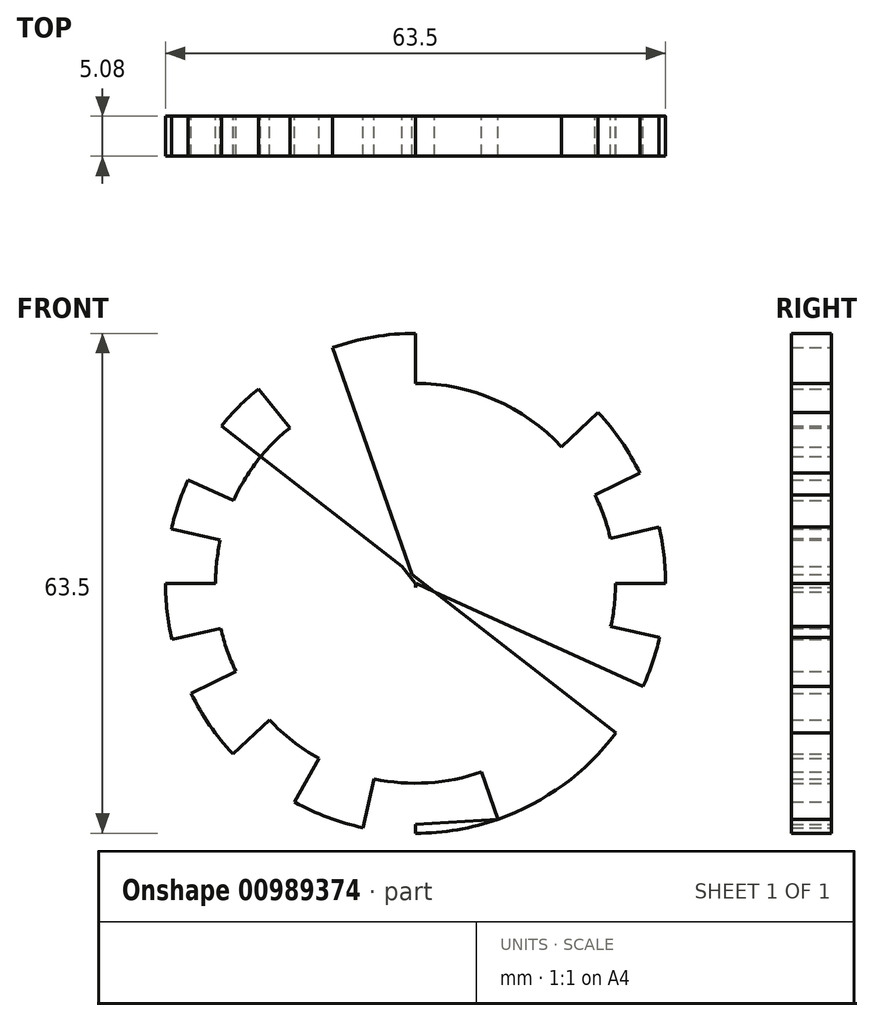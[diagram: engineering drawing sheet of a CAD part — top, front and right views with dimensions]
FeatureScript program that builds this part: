
annotation { "Feature Type Name" : "Feature", "Feature Type Description" : "" }
export const myFeature = defineFeature(function(context is Context, id is Id, definition is map)
    precondition{}
    {
        {
            var Q0;
            Q0=qCreatedBy(makeId("Front.planeOp"),FACE);
            var sketch = newSketch(context, id + "F0", { "sketchPlane" : qUnion([Q0])});
            skCircle(sketch, "E0", {"center": v(0, 0) * mm, "radius": 31.75 * mm});
            skLineSegment(sketch, "E1", {"start": v(-31.75, 0) * mm, "end": v(31.75, 0) * mm});
            skLineSegment(sketch, "E2", {"start": v(-19.95, 24.7) * mm, "end": v(19.95, -24.7) * mm});
            skLineSegment(sketch, "E3", {"start": v(-15.35, -27.8) * mm, "end": v(15.35, 27.8) * mm});
            skCircle(sketch, "E4", {"center": v(0, 0) * mm, "radius": 25.4 * mm});
            skLineSegment(sketch, "E5", {"start": v(-28.91, 13.12) * mm, "end": v(28.91, -13.12) * mm});
            skLineSegment(sketch, "E6", {"start": v(-28.5, -14) * mm, "end": v(28.5, 14) * mm});
            skLineSegment(sketch, "E7", {"start": v(0, -31.75) * mm, "end": v(0, 31.75) * mm});
            skLineSegment(sketch, "E8", {"start": v(-10.56, 29.94) * mm, "end": v(10.5, -29.96) * mm});
            skLineSegment(sketch, "E9", {"start": v(10.5, -29.96) * mm, "end": v(-6.65, -31.04) * mm});
            skLineSegment(sketch, "E10", {"start": v(-6.65, -31.04) * mm, "end": v(6.89, 31) * mm});
            skLineSegment(sketch, "E11", {"start": v(-23.2, -21.67) * mm, "end": v(23.2, 21.67) * mm});
            skLineSegment(sketch, "E12", {"start": v(-30.94, -7.14) * mm, "end": v(30.94, 7.14) * mm});
            skLineSegment(sketch, "E13", {"start": v(-24.67, 19.99) * mm, "end": v(25.43, -19) * mm});
            skLineSegment(sketch, "E14", {"start": v(-31, 6.88) * mm, "end": v(31, -6.88) * mm});
            skSolve(sketch);
        }
        {
            var Q0;
            {var subQ0=sQuery(id+"F0.wireOp",EDGE,"E4");var subQ1=sQuery(id+"F0.wireOp",EDGE,"E3");var subQ2=makeQuery(id+"F0.imprint","INTERSECT",VERTEX,{"disambiguationData":[OD(0.0)],"derivedFrom":[subQ1,subQ0]});Q0=makeQuery(id+"F0.imprint","IMPRINT",FACE,{"disambiguationData":[TD([[makeQuery(id+"F0.imprint","IMPRINT",EDGE,{"disambiguationData":[TD([[subQ2,-1.0]])],"derivedFrom":subQ1}),1.0]])]});}
            var Q1;
            {var subQ1=sQuery(id+"F0.wireOp",EDGE,"E3");var subQ7=sQuery(id+"F0.wireOp",EDGE,"E4");var subQ9=makeQuery(id+"F0.imprint","INTERSECT",VERTEX,{"disambiguationData":[OD(0.0)],"derivedFrom":[subQ1,subQ7]});Q1=makeQuery(id+"F0.imprint","IMPRINT",FACE,{"disambiguationData":[TD([[makeQuery(id+"F0.imprint","IMPRINT",EDGE,{"disambiguationData":[TD([[subQ9,-1.0]])],"derivedFrom":subQ1}),-1.0]])]});}
            var Q2;
            {var subQ0=sQuery(id+"F0.wireOp",EDGE,"E10");var subQ1=sQuery(id+"F0.wireOp",EDGE,"E4");var subQ2=makeQuery(id+"F0.imprint","INTERSECT",VERTEX,{"disambiguationData":[OD(1.0)],"derivedFrom":[subQ1,subQ0]});Q2=makeQuery(id+"F0.imprint","IMPRINT",FACE,{"disambiguationData":[TD([[makeQuery(id+"F0.imprint","IMPRINT",EDGE,{"disambiguationData":[TD([[subQ2,-1.0]])],"derivedFrom":subQ1}),1.0]])]});}
            var Q3;
            {var subQ0=sQuery(id+"F0.wireOp",EDGE,"E7");var subQ1=sQuery(id+"F0.wireOp",EDGE,"E4");var subQ2=makeQuery(id+"F0.imprint","INTERSECT",VERTEX,{"disambiguationData":[OD(1.0)],"derivedFrom":[subQ1,subQ0]});Q3=makeQuery(id+"F0.imprint","IMPRINT",FACE,{"disambiguationData":[TD([[makeQuery(id+"F0.imprint","IMPRINT",EDGE,{"disambiguationData":[TD([[subQ2,-1.0]])],"derivedFrom":subQ1}),1.0]])]});}
            var Q4;
            {var subQ0=sQuery(id+"F0.wireOp",EDGE,"E10");var subQ1=sQuery(id+"F0.wireOp",EDGE,"E2");var subQ2=makeQuery(id+"F0.imprint","INTERSECT",VERTEX,{"derivedFrom":[subQ1,subQ0]});Q4=makeQuery(id+"F0.imprint","IMPRINT",FACE,{"disambiguationData":[TD([[makeQuery(id+"F0.imprint","IMPRINT",EDGE,{"disambiguationData":[TD([[subQ2,-1.0]])],"derivedFrom":subQ1}),-1.0]])]});}
            var Q5;
            {var subQ0=sQuery(id+"F0.wireOp",EDGE,"E10");var subQ6=sQuery(id+"F0.wireOp",EDGE,"E2");var subQ9=makeQuery(id+"F0.imprint","INTERSECT",VERTEX,{"derivedFrom":[subQ6,subQ0]});Q5=makeQuery(id+"F0.imprint","IMPRINT",FACE,{"disambiguationData":[TD([[makeQuery(id+"F0.imprint","IMPRINT",EDGE,{"disambiguationData":[TD([[subQ9,-1.0]])],"derivedFrom":subQ6}),1.0]])]});}
            var Q6;
            {var subQ0=sQuery(id+"F0.wireOp",EDGE,"E13");var subQ1=sQuery(id+"F0.wireOp",EDGE,"E4");var subQ2=makeQuery(id+"F0.imprint","INTERSECT",VERTEX,{"disambiguationData":[OD(1.0)],"derivedFrom":[subQ1,subQ0]});Q6=makeQuery(id+"F0.imprint","IMPRINT",FACE,{"disambiguationData":[TD([[makeQuery(id+"F0.imprint","IMPRINT",EDGE,{"disambiguationData":[TD([[subQ2,-1.0]])],"derivedFrom":subQ1}),1.0]])]});}
            var Q7;
            {var subQ0=sQuery(id+"F0.wireOp",EDGE,"E5");var subQ1=sQuery(id+"F0.wireOp",EDGE,"E4");var subQ2=makeQuery(id+"F0.imprint","INTERSECT",VERTEX,{"disambiguationData":[OD(1.0)],"derivedFrom":[subQ1,subQ0]});Q7=makeQuery(id+"F0.imprint","IMPRINT",FACE,{"disambiguationData":[TD([[makeQuery(id+"F0.imprint","IMPRINT",EDGE,{"disambiguationData":[TD([[subQ2,-1.0]])],"derivedFrom":subQ1}),1.0]])]});}
            var Q8;
            {var subQ0=sQuery(id+"F0.wireOp",EDGE,"E13");var subQ1=sQuery(id+"F0.wireOp",EDGE,"E1");var subQ2=makeQuery(id+"F0.imprint","INTERSECT",VERTEX,{"derivedFrom":[subQ1,subQ0]});Q8=makeQuery(id+"F0.imprint","IMPRINT",FACE,{"disambiguationData":[TD([[makeQuery(id+"F0.imprint","IMPRINT",EDGE,{"disambiguationData":[TD([[subQ2,-1.0]])],"derivedFrom":subQ1}),-1.0]])]});}
            var Q9;
            {var subQ0=sQuery(id+"F0.wireOp",EDGE,"E12");var subQ1=sQuery(id+"F0.wireOp",EDGE,"E4");var subQ2=makeQuery(id+"F0.imprint","INTERSECT",VERTEX,{"disambiguationData":[OD(0.0)],"derivedFrom":[subQ1,subQ0]});Q9=makeQuery(id+"F0.imprint","IMPRINT",FACE,{"disambiguationData":[TD([[makeQuery(id+"F0.imprint","IMPRINT",EDGE,{"disambiguationData":[TD([[subQ2,-1.0]])],"derivedFrom":subQ1}),1.0]])]});}
            var Q10;
            {var subQ0=sQuery(id+"F0.wireOp",EDGE,"E13");var subQ1=sQuery(id+"F0.wireOp",EDGE,"E1");var subQ2=makeQuery(id+"F0.imprint","INTERSECT",VERTEX,{"derivedFrom":[subQ1,subQ0]});Q10=makeQuery(id+"F0.imprint","IMPRINT",FACE,{"disambiguationData":[TD([[makeQuery(id+"F0.imprint","IMPRINT",EDGE,{"disambiguationData":[TD([[subQ2,-1.0]])],"derivedFrom":subQ1}),1.0]])]});}
            var Q11;
            {var subQ0=sQuery(id+"F0.wireOp",EDGE,"E6");var subQ1=sQuery(id+"F0.wireOp",EDGE,"E4");var subQ2=makeQuery(id+"F0.imprint","INTERSECT",VERTEX,{"disambiguationData":[OD(0.0)],"derivedFrom":[subQ1,subQ0]});Q11=makeQuery(id+"F0.imprint","IMPRINT",FACE,{"disambiguationData":[TD([[makeQuery(id+"F0.imprint","IMPRINT",EDGE,{"disambiguationData":[TD([[subQ2,-1.0]])],"derivedFrom":subQ1}),1.0]])]});}
            var Q12;
            {var subQ0=sQuery(id+"F0.wireOp",EDGE,"E13");var subQ1=sQuery(id+"F0.wireOp",EDGE,"E3");var subQ2=makeQuery(id+"F0.imprint","INTERSECT",VERTEX,{"derivedFrom":[subQ1,subQ0]});Q12=makeQuery(id+"F0.imprint","IMPRINT",FACE,{"disambiguationData":[TD([[makeQuery(id+"F0.imprint","IMPRINT",EDGE,{"disambiguationData":[TD([[subQ2,-1.0]])],"derivedFrom":subQ1}),-1.0]])]});}
            var Q13;
            {var subQ0=sQuery(id+"F0.wireOp",EDGE,"E13");var subQ1=sQuery(id+"F0.wireOp",EDGE,"E3");var subQ2=makeQuery(id+"F0.imprint","INTERSECT",VERTEX,{"derivedFrom":[subQ1,subQ0]});Q13=makeQuery(id+"F0.imprint","IMPRINT",FACE,{"disambiguationData":[TD([[makeQuery(id+"F0.imprint","IMPRINT",EDGE,{"disambiguationData":[TD([[subQ2,-1.0]])],"derivedFrom":subQ1}),1.0]])]});}
            var Q14;
            {var subQ0=sQuery(id+"F0.wireOp",EDGE,"E10");var subQ1=sQuery(id+"F0.wireOp",EDGE,"E4");var subQ2=makeQuery(id+"F0.imprint","INTERSECT",VERTEX,{"disambiguationData":[OD(0.0)],"derivedFrom":[subQ1,subQ0]});Q14=makeQuery(id+"F0.imprint","IMPRINT",FACE,{"disambiguationData":[TD([[makeQuery(id+"F0.imprint","IMPRINT",EDGE,{"disambiguationData":[TD([[subQ2,-1.0]])],"derivedFrom":subQ1}),1.0]])]});}
            var Q15;
            {var subQ0=sQuery(id+"F0.wireOp",EDGE,"E7");var subQ1=sQuery(id+"F0.wireOp",EDGE,"E4");var subQ2=makeQuery(id+"F0.imprint","INTERSECT",VERTEX,{"disambiguationData":[OD(0.0)],"derivedFrom":[subQ1,subQ0]});Q15=makeQuery(id+"F0.imprint","IMPRINT",FACE,{"disambiguationData":[TD([[makeQuery(id+"F0.imprint","IMPRINT",EDGE,{"disambiguationData":[TD([[subQ2,-1.0]])],"derivedFrom":subQ1}),1.0]])]});}
            var Q16;
            {var subQ0=sQuery(id+"F0.wireOp",EDGE,"E4");var subQ1=sQuery(id+"F0.wireOp",EDGE,"E2");var subQ2=makeQuery(id+"F0.imprint","INTERSECT",VERTEX,{"disambiguationData":[OD(0.0)],"derivedFrom":[subQ1,subQ0]});Q16=makeQuery(id+"F0.imprint","IMPRINT",FACE,{"disambiguationData":[TD([[makeQuery(id+"F0.imprint","IMPRINT",EDGE,{"disambiguationData":[TD([[subQ2,-1.0]])],"derivedFrom":subQ1}),1.0]])]});}
            var Q17;
            {var subQ0=sQuery(id+"F0.wireOp",EDGE,"E4");var subQ1=sQuery(id+"F0.wireOp",EDGE,"E2");var subQ2=makeQuery(id+"F0.imprint","INTERSECT",VERTEX,{"disambiguationData":[OD(0.0)],"derivedFrom":[subQ1,subQ0]});Q17=makeQuery(id+"F0.imprint","IMPRINT",FACE,{"disambiguationData":[TD([[makeQuery(id+"F0.imprint","IMPRINT",EDGE,{"disambiguationData":[TD([[subQ2,-1.0]])],"derivedFrom":subQ1}),-1.0]])]});}
            var Q18;
            {var subQ5=sQuery(id+"F0.wireOp",EDGE,"E13");var subQ6=sQuery(id+"F0.wireOp",EDGE,"E2");var subQ7=makeQuery(id+"F0.imprint","INTERSECT",VERTEX,{"derivedFrom":[subQ6,subQ5]});Q18=makeQuery(id+"F0.imprint","IMPRINT",FACE,{"disambiguationData":[TD([[makeQuery(id+"F0.imprint","IMPRINT",EDGE,{"disambiguationData":[TD([[subQ7,-1.0]])],"derivedFrom":subQ6}),-1.0]])]});}
            var Q19;
            {var subQ0=sQuery(id+"F0.wireOp",EDGE,"E5");var subQ1=sQuery(id+"F0.wireOp",EDGE,"E4");var subQ2=makeQuery(id+"F0.imprint","INTERSECT",VERTEX,{"disambiguationData":[OD(0.0)],"derivedFrom":[subQ1,subQ0]});Q19=makeQuery(id+"F0.imprint","IMPRINT",FACE,{"disambiguationData":[TD([[makeQuery(id+"F0.imprint","IMPRINT",EDGE,{"disambiguationData":[TD([[subQ2,-1.0]])],"derivedFrom":subQ1}),1.0]])]});}
            var Q20;
            {var subQ0=sQuery(id+"F0.wireOp",EDGE,"E4");var subQ1=sQuery(id+"F0.wireOp",EDGE,"E1");var subQ2=makeQuery(id+"F0.imprint","INTERSECT",VERTEX,{"disambiguationData":[OD(0.0)],"derivedFrom":[subQ1,subQ0]});Q20=makeQuery(id+"F0.imprint","IMPRINT",FACE,{"disambiguationData":[TD([[makeQuery(id+"F0.imprint","IMPRINT",EDGE,{"disambiguationData":[TD([[subQ2,-1.0]])],"derivedFrom":subQ1}),1.0]])]});}
            var Q21;
            {var subQ0=sQuery(id+"F0.wireOp",EDGE,"E4");var subQ1=sQuery(id+"F0.wireOp",EDGE,"E1");var subQ2=makeQuery(id+"F0.imprint","INTERSECT",VERTEX,{"disambiguationData":[OD(0.0)],"derivedFrom":[subQ1,subQ0]});Q21=makeQuery(id+"F0.imprint","IMPRINT",FACE,{"disambiguationData":[TD([[makeQuery(id+"F0.imprint","IMPRINT",EDGE,{"disambiguationData":[TD([[subQ2,-1.0]])],"derivedFrom":subQ1}),-1.0]])]});}
            var Q22;
            {var subQ0=sQuery(id+"F0.wireOp",EDGE,"E12");var subQ1=sQuery(id+"F0.wireOp",EDGE,"E4");var subQ2=makeQuery(id+"F0.imprint","INTERSECT",VERTEX,{"disambiguationData":[OD(1.0)],"derivedFrom":[subQ1,subQ0]});Q22=makeQuery(id+"F0.imprint","IMPRINT",FACE,{"disambiguationData":[TD([[makeQuery(id+"F0.imprint","IMPRINT",EDGE,{"disambiguationData":[TD([[subQ2,-1.0]])],"derivedFrom":subQ1}),1.0]])]});}
            var Q23;
            {var subQ0=sQuery(id+"F0.wireOp",EDGE,"E6");var subQ1=sQuery(id+"F0.wireOp",EDGE,"E4");var subQ2=makeQuery(id+"F0.imprint","INTERSECT",VERTEX,{"disambiguationData":[OD(1.0)],"derivedFrom":[subQ1,subQ0]});Q23=makeQuery(id+"F0.imprint","IMPRINT",FACE,{"disambiguationData":[TD([[makeQuery(id+"F0.imprint","IMPRINT",EDGE,{"disambiguationData":[TD([[subQ2,-1.0]])],"derivedFrom":subQ1}),1.0]])]});}
            var Q24;
            {var subQ0=sQuery(id+"F0.wireOp",EDGE,"E7");var subQ1=sQuery(id+"F0.wireOp",EDGE,"E4");var subQ2=makeQuery(id+"F0.imprint","INTERSECT",VERTEX,{"disambiguationData":[OD(1.0)],"derivedFrom":[subQ1,subQ0]});Q24=makeQuery(id+"F0.imprint","IMPRINT",FACE,{"disambiguationData":[TD([[makeQuery(id+"F0.imprint","IMPRINT",EDGE,{"disambiguationData":[TD([[subQ2,-1.0]])],"derivedFrom":subQ1}),-1.0]])]});}
            var Q25;
            {var subQ0=sQuery(id+"F0.wireOp",EDGE,"E7");var subQ1=sQuery(id+"F0.wireOp",EDGE,"E0");var subQ2=makeQuery(id+"F0.imprint","INTERSECT",VERTEX,{"disambiguationData":[OD(0.0)],"derivedFrom":[subQ1,subQ0]});Q25=makeQuery(id+"F0.imprint","IMPRINT",FACE,{"disambiguationData":[TD([[makeQuery(id+"F0.imprint","IMPRINT",EDGE,{"disambiguationData":[TD([[subQ2,-1.0]])],"derivedFrom":subQ0}),-1.0]])]});}
            var Q26;
            {var subQ0=sQuery(id+"F0.wireOp",EDGE,"E2");var subQ1=sQuery(id+"F0.wireOp",EDGE,"E0");var subQ2=makeQuery(id+"F0.imprint","INTERSECT",VERTEX,{"disambiguationData":[OD(1.0)],"derivedFrom":[subQ1,subQ0]});Q26=makeQuery(id+"F0.imprint","IMPRINT",FACE,{"disambiguationData":[TD([[makeQuery(id+"F0.imprint","IMPRINT",EDGE,{"disambiguationData":[TD([[subQ2,-1.0]])],"derivedFrom":subQ1}),1.0]])]});}
            var Q27;
            {var subQ0=sQuery(id+"F0.wireOp",EDGE,"E5");var subQ1=sQuery(id+"F0.wireOp",EDGE,"E0");var subQ2=makeQuery(id+"F0.imprint","INTERSECT",VERTEX,{"disambiguationData":[OD(1.0)],"derivedFrom":[subQ1,subQ0]});Q27=makeQuery(id+"F0.imprint","IMPRINT",FACE,{"disambiguationData":[TD([[makeQuery(id+"F0.imprint","IMPRINT",EDGE,{"disambiguationData":[TD([[subQ2,-1.0]])],"derivedFrom":subQ1}),1.0]])]});}
            var Q28;
            {var subQ0=sQuery(id+"F0.wireOp",EDGE,"E1");var subQ1=sQuery(id+"F0.wireOp",EDGE,"E0");var subQ2=makeQuery(id+"F0.imprint","INTERSECT",VERTEX,{"disambiguationData":[OD(1.0)],"derivedFrom":[subQ1,subQ0]});Q28=makeQuery(id+"F0.imprint","IMPRINT",FACE,{"disambiguationData":[TD([[makeQuery(id+"F0.imprint","IMPRINT",EDGE,{"disambiguationData":[TD([[subQ2,-1.0]])],"derivedFrom":subQ1}),1.0]])]});}
            var Q29;
            {var subQ0=sQuery(id+"F0.wireOp",EDGE,"E6");var subQ1=sQuery(id+"F0.wireOp",EDGE,"E0");var subQ2=makeQuery(id+"F0.imprint","INTERSECT",VERTEX,{"disambiguationData":[OD(1.0)],"derivedFrom":[subQ1,subQ0]});Q29=makeQuery(id+"F0.imprint","IMPRINT",FACE,{"disambiguationData":[TD([[makeQuery(id+"F0.imprint","IMPRINT",EDGE,{"disambiguationData":[TD([[subQ2,-1.0]])],"derivedFrom":subQ1}),1.0]])]});}
            var Q30;
            {var subQ0=sQuery(id+"F0.wireOp",EDGE,"E3");var subQ1=sQuery(id+"F0.wireOp",EDGE,"E0");var subQ2=makeQuery(id+"F0.imprint","INTERSECT",VERTEX,{"disambiguationData":[OD(1.0)],"derivedFrom":[subQ1,subQ0]});Q30=makeQuery(id+"F0.imprint","IMPRINT",FACE,{"disambiguationData":[TD([[makeQuery(id+"F0.imprint","IMPRINT",EDGE,{"disambiguationData":[TD([[subQ2,-1.0]])],"derivedFrom":subQ1}),1.0]])]});}
            var Q31;
            {var subQ0=sQuery(id+"F0.wireOp",EDGE,"E7");var subQ1=sQuery(id+"F0.wireOp",EDGE,"E0");var subQ2=makeQuery(id+"F0.imprint","INTERSECT",VERTEX,{"disambiguationData":[OD(1.0)],"derivedFrom":[subQ1,subQ0]});Q31=makeQuery(id+"F0.imprint","IMPRINT",FACE,{"disambiguationData":[TD([[makeQuery(id+"F0.imprint","IMPRINT",EDGE,{"disambiguationData":[TD([[subQ2,-1.0]])],"derivedFrom":subQ1}),1.0]])]});}
            var Q32;
            {var subQ0=sQuery(id+"F0.wireOp",EDGE,"E2");var subQ1=sQuery(id+"F0.wireOp",EDGE,"E0");var subQ2=makeQuery(id+"F0.imprint","INTERSECT",VERTEX,{"disambiguationData":[OD(0.0)],"derivedFrom":[subQ1,subQ0]});Q32=makeQuery(id+"F0.imprint","IMPRINT",FACE,{"disambiguationData":[TD([[makeQuery(id+"F0.imprint","IMPRINT",EDGE,{"disambiguationData":[TD([[subQ2,-1.0]])],"derivedFrom":subQ1}),1.0]])]});}
            var Q33;
            {var subQ0=sQuery(id+"F0.wireOp",EDGE,"E5");var subQ1=sQuery(id+"F0.wireOp",EDGE,"E0");var subQ2=makeQuery(id+"F0.imprint","INTERSECT",VERTEX,{"disambiguationData":[OD(0.0)],"derivedFrom":[subQ1,subQ0]});Q33=makeQuery(id+"F0.imprint","IMPRINT",FACE,{"disambiguationData":[TD([[makeQuery(id+"F0.imprint","IMPRINT",EDGE,{"disambiguationData":[TD([[subQ2,-1.0]])],"derivedFrom":subQ1}),1.0]])]});}
            var Q34;
            {var subQ0=sQuery(id+"F0.wireOp",EDGE,"E1");var subQ1=sQuery(id+"F0.wireOp",EDGE,"E0");var subQ2=makeQuery(id+"F0.imprint","INTERSECT",VERTEX,{"disambiguationData":[OD(0.0)],"derivedFrom":[subQ1,subQ0]});Q34=makeQuery(id+"F0.imprint","IMPRINT",FACE,{"disambiguationData":[TD([[makeQuery(id+"F0.imprint","IMPRINT",EDGE,{"disambiguationData":[TD([[subQ2,-1.0]])],"derivedFrom":subQ1}),1.0]])]});}
            var Q35;
            {var subQ0=sQuery(id+"F0.wireOp",EDGE,"E6");var subQ1=sQuery(id+"F0.wireOp",EDGE,"E0");var subQ2=makeQuery(id+"F0.imprint","INTERSECT",VERTEX,{"disambiguationData":[OD(0.0)],"derivedFrom":[subQ1,subQ0]});Q35=makeQuery(id+"F0.imprint","IMPRINT",FACE,{"disambiguationData":[TD([[makeQuery(id+"F0.imprint","IMPRINT",EDGE,{"disambiguationData":[TD([[subQ2,-1.0]])],"derivedFrom":subQ1}),1.0]])]});}
            var Q36;
            {var subQ0=sQuery(id+"F0.wireOp",EDGE,"E3");var subQ1=sQuery(id+"F0.wireOp",EDGE,"E0");var subQ2=makeQuery(id+"F0.imprint","INTERSECT",VERTEX,{"disambiguationData":[OD(0.0)],"derivedFrom":[subQ1,subQ0]});Q36=makeQuery(id+"F0.imprint","IMPRINT",FACE,{"disambiguationData":[TD([[makeQuery(id+"F0.imprint","IMPRINT",EDGE,{"disambiguationData":[TD([[subQ2,-1.0]])],"derivedFrom":subQ0}),-1.0]])]});}
            extrude(context, id + "F1", {"entities" : qUnion([Q0, Q1, Q2, Q3, Q4, Q5, Q6, Q7, Q8, Q9, Q10, Q11, Q12, Q13, Q14, Q15, Q16, Q17, Q18, Q19, Q20, Q21, Q22, Q23, Q24, Q25, Q26, Q27, Q28, Q29, Q30, Q31, Q32, Q33, Q34, Q35, Q36]), "depth" : 5.08 * mm, "offsetDistance" : 25.4 * mm});
        }
    });
